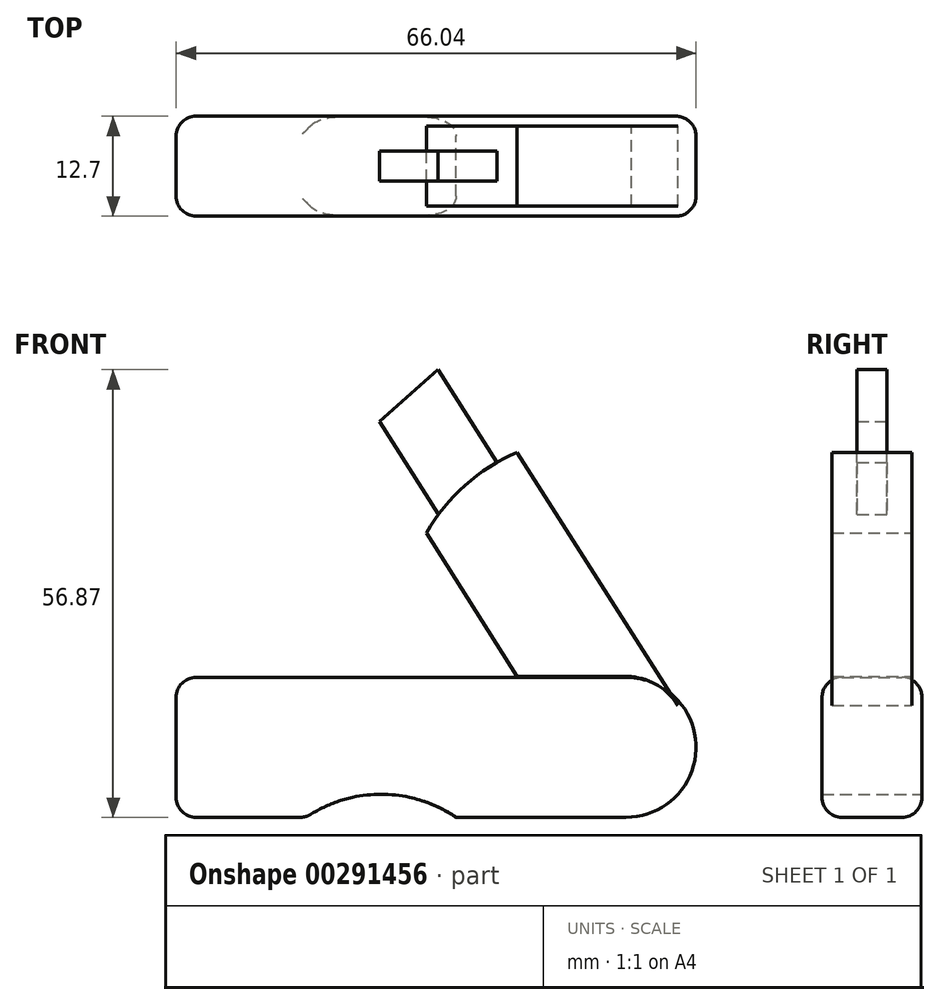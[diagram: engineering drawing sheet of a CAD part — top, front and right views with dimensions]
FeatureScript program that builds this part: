
annotation { "Feature Type Name" : "Feature", "Feature Type Description" : "" }
export const myFeature = defineFeature(function(context is Context, id is Id, definition is map)
    precondition{}
    {
        {
            var Q0;
            Q0=qCreatedBy(makeId("Front.planeOp"),FACE);
            var sketch = newSketch(context, id + "F0", { "sketchPlane" : qUnion([Q0])});
            skLineSegment(sketch, "E0.top", {"start": v(-28.57, 8.9) * mm, "end": v(28.58, 8.9) * mm});
            skPoint(sketch, "E0.middle", {"position": v(0, 0) * mm});
            skLineSegment(sketch, "E1", {"start": v(-28.57, 8.9) * mm, "end": v(-28.58, -8.9) * mm});
            skArc(sketch, "E2", {"start": v(28.58, -8.9) * mm, "mid": v(37.47, 0) * mm, "end": v(28.58, 8.9) * mm});
            skLineSegment(sketch, "E3", {"start": v(-28.58, -8.9) * mm, "end": v(-12.07, -8.9) * mm});
            skArc(sketch, "E4", {"start": v(6.99, -8.9) * mm, "mid": v(-2.54, -5.96) * mm, "end": v(-12.07, -8.9) * mm});
            skLineSegment(sketch, "E5", {"start": v(6.99, -8.9) * mm, "end": v(28.58, -8.89) * mm});
            skSolve(sketch);
        }
        {
            var Q0;
            Q0=qCreatedBy(makeId("Front.planeOp"),FACE);
            var sketch = newSketch(context, id + "F1", { "sketchPlane" : qUnion([Q0])});
            skLineSegment(sketch, "E6", {"start": v(35.17, 5.35) * mm, "end": v(14.7, 37.48) * mm});
            skLineSegment(sketch, "E7", {"start": v(3.21, 27.26) * mm, "end": v(14.7, 8.98) * mm});
            skArc(sketch, "E8", {"start": v(14.7, 37.48) * mm, "mid": v(8.14, 33.28) * mm, "end": v(3.21, 27.26) * mm});
            skLineSegment(sketch, "E9", {"start": v(14.7, 8.98) * mm, "end": v(29.25, 8.98) * mm});
            skArc(sketch, "E10", {"start": v(35.17, 5.35) * mm, "mid": v(32.63, 7.84) * mm, "end": v(29.25, 8.98) * mm});
            skLineSegment(sketch, "E11", {"start": v(12.18, 36.2) * mm, "end": v(4.67, 47.98) * mm});
            skLineSegment(sketch, "E12", {"start": v(4.76, 29.6) * mm, "end": v(-2.75, 41.38) * mm});
            skLineSegment(sketch, "E13", {"start": v(4.67, 47.98) * mm, "end": v(-2.75, 41.38) * mm});
            skSolve(sketch);
        }
        {
            var Q0;
            Q0=makeQuery(id+"F0.imprint","IMPRINT",FACE,{"disambiguationData":[TD([[makeQuery(id+"F0.imprint","IMPRINT",EDGE,{"derivedFrom":sQuery(id+"F0.wireOp",EDGE,"E0.top")}),-1.0]])]});
            extrude(context, id + "F2", {"entities" : qUnion([Q0]), "endBound" : BoundingType.SYMMETRIC, "depth" : 12.7 * mm});
        }
        {
            var Q0;
            {var subQ0=sQuery(id+"F1.wireOp",EDGE,"E11");Q0=makeQuery(id+"F1.imprint","IMPRINT",FACE,{"disambiguationData":[TD([[makeQuery(id+"F1.imprint","IMPRINT",EDGE,{"derivedFrom":subQ0}),1.0]])]});}
            extrude(context, id + "F3", {"entities" : qUnion([Q0]), "operationType" : NewBodyOperationType.ADD, "endBound" : BoundingType.SYMMETRIC, "depth" : 3.8 * mm});
        }
        {
            var Q0;
            {var subQ3=sQuery(id+"F1.wireOp",EDGE,"E6");Q0=makeQuery(id+"F1.imprint","IMPRINT",FACE,{"disambiguationData":[TD([[makeQuery(id+"F1.imprint","IMPRINT",EDGE,{"derivedFrom":subQ3}),1.0]])]});}
            extrude(context, id + "F4", {"entities" : qUnion([Q0]), "endBound" : BoundingType.SYMMETRIC, "depth" : 10.16 * mm});
        }
        {
            var Q0;
            Q0=makeQuery(id+"F2.opExtrude","SWEPT_FACE",FACE,{"disambiguationData":[OSD([sQuery(id+"F0.wireOp",EDGE,"E1")])]});
            var Q1;
            Q1=makeQuery(id+"F2.opExtrude","SWEPT_FACE",FACE,{"disambiguationData":[OSD([sQuery(id+"F0.wireOp",EDGE,"E0.top")])]});
            var Q2;
            Q2=makeQuery(id+"F2.opExtrude","SWEPT_FACE",FACE,{"disambiguationData":[OSD([sQuery(id+"F0.wireOp",EDGE,"E3")])]});
            fillet(context, id + "F5", {"entities" : qUnion([Q0, Q1, Q2]), "radius" : 2.54 * mm, "tangentPropagation" : true, "allowEdgeOverflow" : false});
        }
    });
